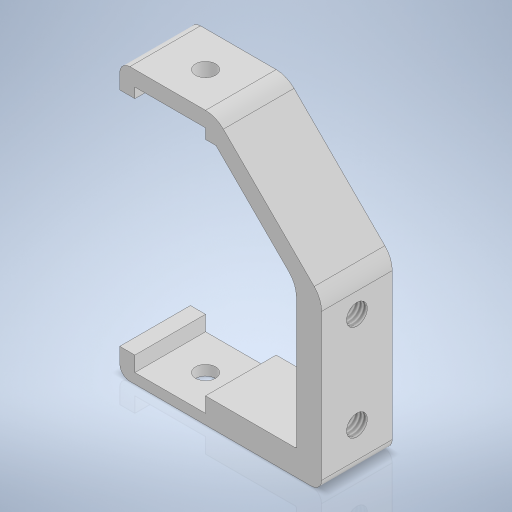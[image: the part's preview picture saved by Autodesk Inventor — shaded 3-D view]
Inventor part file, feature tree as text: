
AUTODESK INVENTOR PART (.ipt)
format: ipt  version: 2024 (Build 280153000, 153)  size: 312,832 bytes
history: native  units: mm
features: sketch x4, hole x3, fillet x2, extrude x1, projected_geometry x1
ambient origin geometry x8: Origin, YZ Plane, XZ Plane, XY Plane, X Axis, Y Axis, Z Axis, Center Point
bodies: Volumenkörper1 (feature_tree)
feature tree (11):
  extrude  "Extrusion1"  Depth=40.0mm
  fillet  "Rundung1"  Radius=3.0mm
  fillet  "Rundung2"  Radius=14.0mm
  hole  "Bohrung1"  [1 undecoded]
  hole  "Bohrung2"  [1 undecoded]
  hole  "Bohrung3"  [1 undecoded]
  sketch  "Skizze1"  dims[d2=5.0mm d3=40.0mm d4=3.0mm d5=14.0mm]
  sketch  "Skizze2"  dims[d6=54.0mm d7=3.0mm]
  sketch  "Skizze3"  dims[d8=2.0mm d12=26.0mm]
  projected_geometry  "Projizierte Kontur1"
  sketch  "Skizze5"  dims[d16=2.0mm d17=3.0mm d18=5.0mm d19=5.0mm d20=5.0mm d21=45.0deg d22=14.0mm d23=0.0mm d24=2.0mm d25=0.2mm d26=19.0mm d27=8.0mm d28=4.134mm d29=10.0mm d30=4.0mm d31=2.0mm d32=90.0deg d33=8.0mm d34=0.0mm d35=4.0mm d36=10.0mm d37=4.0mm d38=2.0mm d39=90.0deg d40=8.0mm d41=0.0mm d42=10.0mm d44=10.0mm d45=4.0mm d46=6.0mm d47=4.0mm d48=2.0mm d49=90.0deg d50=8.0mm d51=0.0mm]
note: 3 required parameter values undecoded (feature->parameter linkage not recoverable at this tier; creation-order binding heuristic only, values carry confidence <= 0.55)
